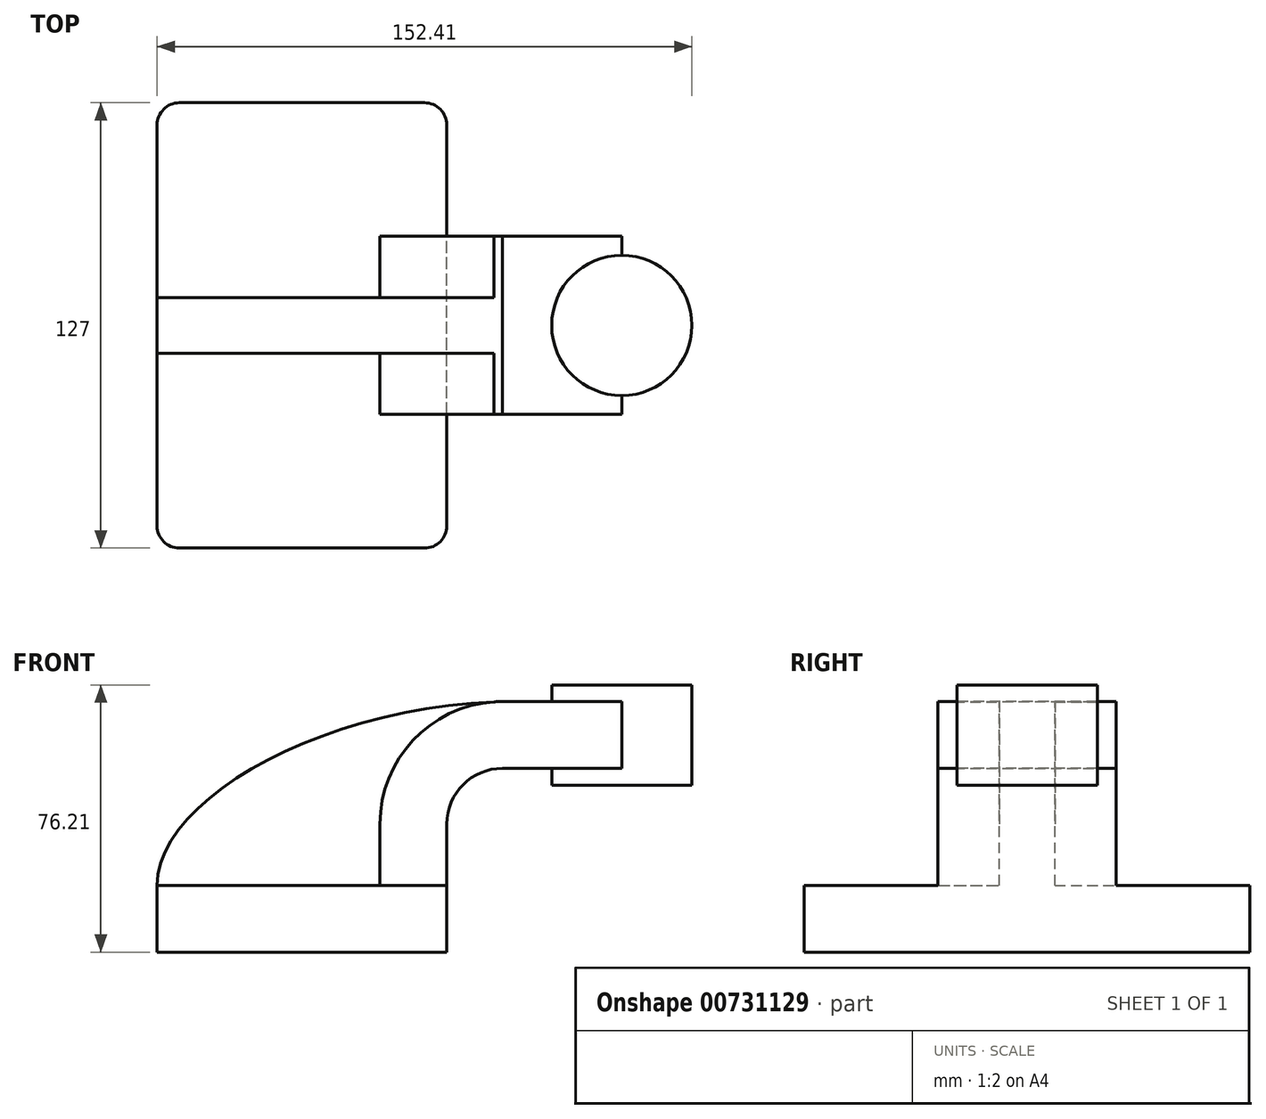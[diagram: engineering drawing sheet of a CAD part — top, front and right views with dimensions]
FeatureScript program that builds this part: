
annotation { "Feature Type Name" : "Feature", "Feature Type Description" : "" }
export const myFeature = defineFeature(function(context is Context, id is Id, definition is map)
    precondition{}
    {
        {
            var Q0;
            Q0=qCreatedBy(makeId("Front.planeOp"),FACE);
            var sketch = newSketch(context, id + "F0", { "sketchPlane" : qUnion([Q0])});
            skLineSegment(sketch, "E0.bottom", {"start": v(41.27, 9.53) * mm, "end": v(-41.28, 9.53) * mm});
            skLineSegment(sketch, "E0.top", {"start": v(41.28, -9.52) * mm, "end": v(-41.27, -9.52) * mm});
            skLineSegment(sketch, "E0.left", {"start": v(41.28, 9.53) * mm, "end": v(41.28, -9.52) * mm});
            skLineSegment(sketch, "E0.right", {"start": v(-41.28, 9.53) * mm, "end": v(-41.28, -9.52) * mm});
            skPoint(sketch, "E0.middle", {"position": v(0, 0) * mm});
            skLineSegment(sketch, "E1.bottom", {"start": v(60.32, 38.1) * mm, "end": v(111.12, 38.1) * mm});
            skLineSegment(sketch, "E1.top", {"start": v(60.32, 66.68) * mm, "end": v(111.12, 66.68) * mm});
            skLineSegment(sketch, "E1.left", {"start": v(60.32, 38.1) * mm, "end": v(60.32, 66.68) * mm});
            skLineSegment(sketch, "E1.right", {"start": v(111.12, 38.1) * mm, "end": v(111.12, 66.68) * mm});
            skPoint(sketch, "E1.middle", {"position": v(85.72, 52.39) * mm});
            skLineSegment(sketch, "E2", {"start": v(41.27, 9.53) * mm, "end": v(41.27, 27) * mm});
            skArc(sketch, "E3", {"start": v(41.27, 27) * mm, "mid": v(45.92, 38.23) * mm, "end": v(57.15, 42.88) * mm});
            skLineSegment(sketch, "E4", {"start": v(57.15, 42.88) * mm, "end": v(91.14, 42.88) * mm});
            skLineSegment(sketch, "E5.0", {"start": v(57.15, 61.93) * mm, "end": v(91.14, 61.93) * mm});
            skArc(sketch, "E5.1", {"start": v(22.22, 27) * mm, "mid": v(32.45, 51.7) * mm, "end": v(57.15, 61.93) * mm});
            skLineSegment(sketch, "E5.2", {"start": v(22.22, 9.53) * mm, "end": v(22.22, 27) * mm});
            skLineSegment(sketch, "E6", {"start": v(91.14, 42.88) * mm, "end": v(91.14, 66.68) * mm});
            skFitSpline(sketch, "E7", {"points": [v(-41.28, 9.53) * mm, v(57.15, 61.93) * mm], "startDerivative": vector(0.17, 73.88) * mm, "endDerivative": vector(153.24, 4.1) * mm});
            skLineSegment(sketch, "E8", {"start": v(91.14, 66.68) * mm, "end": v(91.14, 38.1) * mm});
            skSolve(sketch);
        }
        {
            var Q0;
            Q0=makeQuery(id+"F0.imprint","IMPRINT",FACE,{"disambiguationData":[TD([[makeQuery(id+"F0.imprint","IMPRINT",EDGE,{"derivedFrom":sQuery(id+"F0.wireOp",EDGE,"E0.top")}),-1.0]])]});
            extrude(context, id + "F1", {"entities" : qUnion([Q0]), "endBound" : BoundingType.SYMMETRIC, "depth" : 127 * mm, "offsetDistance" : 25.4 * mm});
        }
        {
            var Q0;
            {var subQ6=sQuery(id+"F0.wireOp",EDGE,"E2");Q0=makeQuery(id+"F0.imprint","IMPRINT",FACE,{"disambiguationData":[TD([[makeQuery(id+"F0.imprint","IMPRINT",EDGE,{"derivedFrom":subQ6}),1.0]])]});}
            var Q1;
            {var subQ0=sQuery(id+"F0.wireOp",EDGE,"E4");var subQ1=sQuery(id+"F0.wireOp",EDGE,"E1.left");var subQ2=makeQuery(id+"F0.imprint","INTERSECT",VERTEX,{"derivedFrom":[subQ1,subQ0]});Q1=makeQuery(id+"F0.imprint","IMPRINT",FACE,{"disambiguationData":[TD([[makeQuery(id+"F0.imprint","IMPRINT",EDGE,{"disambiguationData":[TD([[subQ2,-1.0]])],"derivedFrom":subQ1}),-1.0]])]});}
            extrude(context, id + "F2", {"entities" : qUnion([Q0, Q1]), "operationType" : NewBodyOperationType.ADD, "endBound" : BoundingType.SYMMETRIC, "depth" : 50.8 * mm, "offsetDistance" : 25.4 * mm});
        }
        {
            var Q0;
            {var subQ3=sQuery(id+"F0.wireOp",EDGE,"E5.2");Q0=makeQuery(id+"F0.imprint","IMPRINT",FACE,{"disambiguationData":[TD([[makeQuery(id+"F0.imprint","IMPRINT",EDGE,{"derivedFrom":subQ3}),1.0]])]});}
            extrude(context, id + "F3", {"entities" : qUnion([Q0]), "operationType" : NewBodyOperationType.ADD, "endBound" : BoundingType.SYMMETRIC, "depth" : 15.88 * mm, "offsetDistance" : 25.4 * mm});
        }
        {
            var Q0;
            {var subQ4=sQuery(id+"F0.wireOp",EDGE,"E1.right");Q0=makeQuery(id+"F0.imprint","IMPRINT",FACE,{"disambiguationData":[TD([[makeQuery(id+"F0.imprint","IMPRINT",EDGE,{"derivedFrom":subQ4}),1.0]])]});}
            var Q1;
            Q1=sQuery(id+"F0.wireOp",EDGE,"E8");
            revolve(context, id + "F4", {"operationType" : NewBodyOperationType.ADD, "surfaceOperationType" : NewSurfaceOperationType.NEW, "entities" : qUnion([Q0]), "axis" : qUnion([Q1]), "revolveType" : RevolveType.FULL});
        }
        {
            var Q0;
            Q0=makeQuery(id+"F1.opExtrude","CAP_EDGE",EDGE,{"disambiguationData":[OSD([sQuery(id+"F0.wireOp",EDGE,"E0.left")])],"isStart":false});
            var Q1;
            Q1=makeQuery(id+"F1.opExtrude","CAP_EDGE",EDGE,{"disambiguationData":[OSD([sQuery(id+"F0.wireOp",EDGE,"E0.right")])],"isStart":false});
            var Q2;
            Q2=makeQuery(id+"F1.opExtrude","CAP_EDGE",EDGE,{"disambiguationData":[OSD([sQuery(id+"F0.wireOp",EDGE,"E0.right")])],"isStart":true});
            var Q3;
            Q3=makeQuery(id+"F1.opExtrude","CAP_EDGE",EDGE,{"disambiguationData":[OSD([sQuery(id+"F0.wireOp",EDGE,"E0.left")])],"isStart":true});
            fillet(context, id + "F5", {"entities" : qUnion([Q0, Q1, Q2, Q3]), "radius" : 6.35 * mm, "tangentPropagation" : true, "allowEdgeOverflow" : false});
        }
    });
